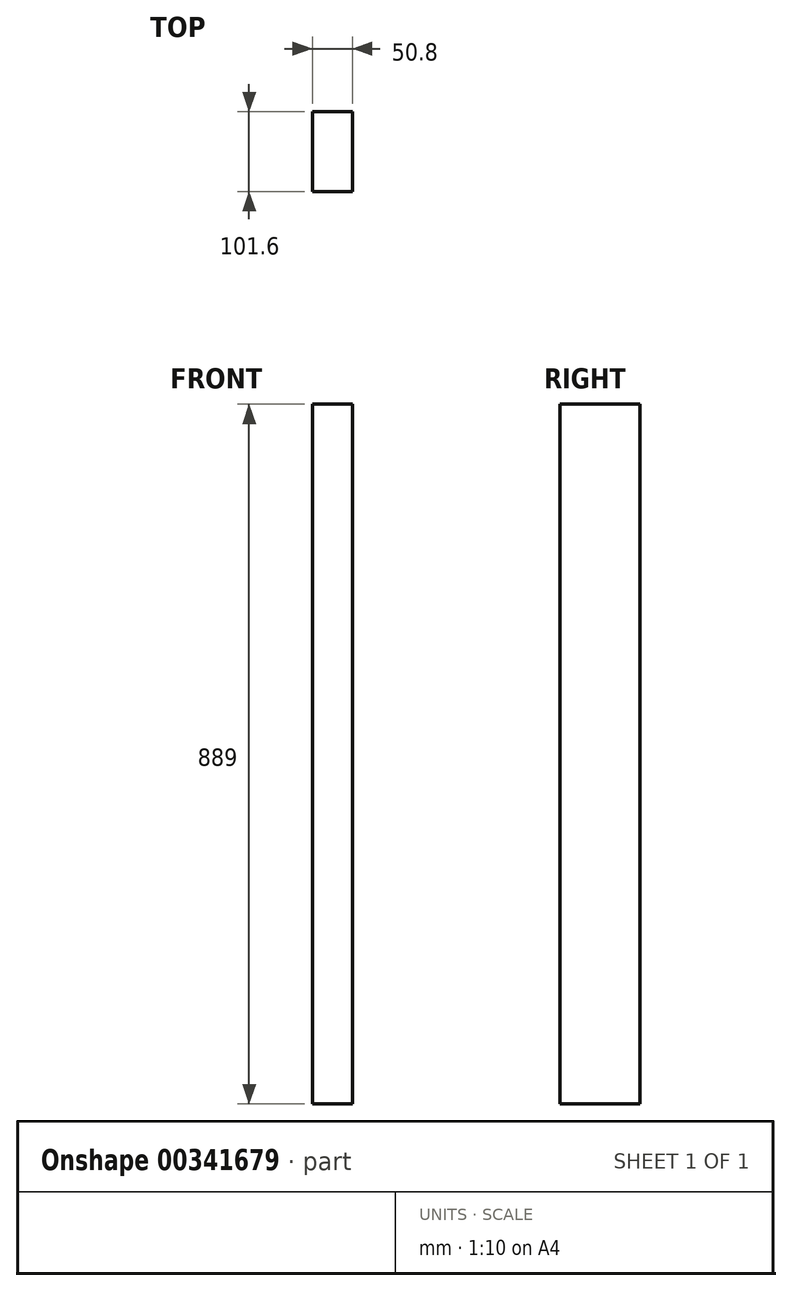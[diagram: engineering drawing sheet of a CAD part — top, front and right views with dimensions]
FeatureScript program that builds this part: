
annotation { "Feature Type Name" : "Feature", "Feature Type Description" : "" }
export const myFeature = defineFeature(function(context is Context, id is Id, definition is map)
    precondition{}
    {
        {
            var Q0;
            Q0=qCreatedBy(makeId("Right.planeOp"),FACE);
            var sketch = newSketch(context, id + "F0", { "sketchPlane" : qUnion([Q0])});
            skLineSegment(sketch, "E0.bottom", {"start": v(-93.53, 444.07) * mm, "end": v(8.07, 444.07) * mm});
            skLineSegment(sketch, "E0.top", {"start": v(-93.53, -444.93) * mm, "end": v(8.07, -444.93) * mm});
            skLineSegment(sketch, "E0.left", {"start": v(-93.53, 444.07) * mm, "end": v(-93.53, -444.93) * mm});
            skLineSegment(sketch, "E0.right", {"start": v(8.07, 444.07) * mm, "end": v(8.07, -444.93) * mm});
            skSolve(sketch);
        }
        {
            var Q0;
            Q0=makeQuery(id+"F0.imprint","IMPRINT",FACE,{"disambiguationData":[TD([[makeQuery(id+"F0.imprint","IMPRINT",EDGE,{"derivedFrom":sQuery(id+"F0.wireOp",EDGE,"E0.bottom")}),-1.0]])]});
            extrude(context, id + "F1", {"entities" : qUnion([Q0]), "depth" : 50.8 * mm});
        }
    });
